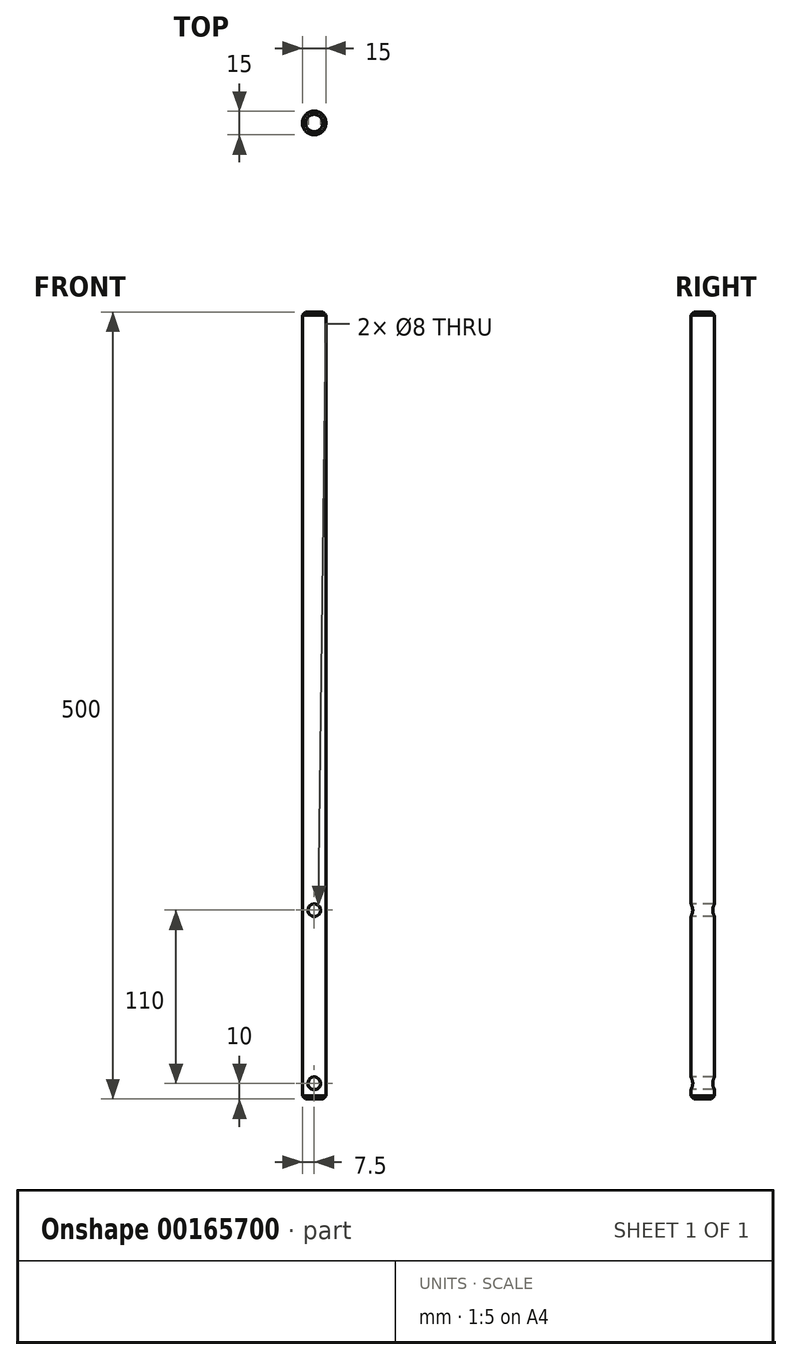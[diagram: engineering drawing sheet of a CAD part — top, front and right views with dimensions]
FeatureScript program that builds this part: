
annotation { "Feature Type Name" : "Feature", "Feature Type Description" : "" }
export const myFeature = defineFeature(function(context is Context, id is Id, definition is map)
    precondition{}
    {
        {
            var Q0;
            Q0=qCreatedBy(makeId("Top.planeOp"),FACE);
            var sketch = newSketch(context, id + "F0", { "sketchPlane" : qUnion([Q0])});
            skCircle(sketch, "E0", {"center": v(0, 0) * mm, "radius": 7.5 * mm});
            skSolve(sketch);
        }
        {
            var Q0;
            Q0=makeQuery(id+"F0.imprint","IMPRINT",FACE,{"disambiguationData":[TD([[makeQuery(id+"F0.imprint","IMPRINT",EDGE,{"derivedFrom":sQuery(id+"F0.wireOp",EDGE,"E0")}),1.0]])]});
            extrude(context, id + "F1", {"entities" : qUnion([Q0]), "depth" : 500 * mm, "offsetDistance" : 25 * mm});
        }
        {
            var Q0;
            Q0=makeQuery(id+"F1.opExtrude","CAP_EDGE",EDGE,{"disambiguationData":[OSD([sQuery(id+"F0.wireOp",EDGE,"E0")])],"isStart":true});
            var Q1;
            Q1=makeQuery(id+"F1.opExtrude","CAP_EDGE",EDGE,{"disambiguationData":[OSD([sQuery(id+"F0.wireOp",EDGE,"E0")])],"isStart":false});
            chamfer(context, id + "F2", {"entities" : qUnion([Q0, Q1]), "width" : 2 * mm, "tangentPropagation" : true});
        }
        {
            var Q0;
            Q0=qCreatedBy(makeId("Front.planeOp"),FACE);
            var sketch = newSketch(context, id + "F3", { "sketchPlane" : qUnion([Q0])});
            skCircle(sketch, "E1", {"center": v(0, 10) * mm, "radius": 4 * mm});
            skCircle(sketch, "E2", {"center": v(0, 120) * mm, "radius": 4 * mm});
            skSolve(sketch);
        }
        {
            var Q0;
            Q0 = qSketchRegion(id + "F3", true);
            extrude(context, id + "F4", {"entities" : qUnion([Q0]), "operationType" : NewBodyOperationType.REMOVE, "endBound" : BoundingType.SYMMETRIC, "oppositeDirection" : true, "depth" : 20 * mm, "offsetDistance" : 25 * mm});
        }
    });
